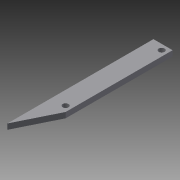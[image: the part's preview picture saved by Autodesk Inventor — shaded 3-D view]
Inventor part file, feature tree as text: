
AUTODESK INVENTOR PART (.ipt)
format: ipt  version: 2013 (Build 170138000, 138)  size: 72,704 bytes
history: native  units: in
note: dims shown in document units (in); Inventor stores cm internally (conversion verified against a paired STEP export)
features: extrude x1, sketch x1
ambient origin geometry x8: Origin, YZ Plane, XZ Plane, XY Plane, X Axis, Y Axis, Z Axis, Center Point
bodies: Solid1 (feature_tree)
feature tree (2):
  extrude  "Extrusion1"  Depth=0.25in TaperAngle=0.0deg
  sketch  "Sketch1"  dims[d0=0.875in d1=0.25in d2=0.0in]
